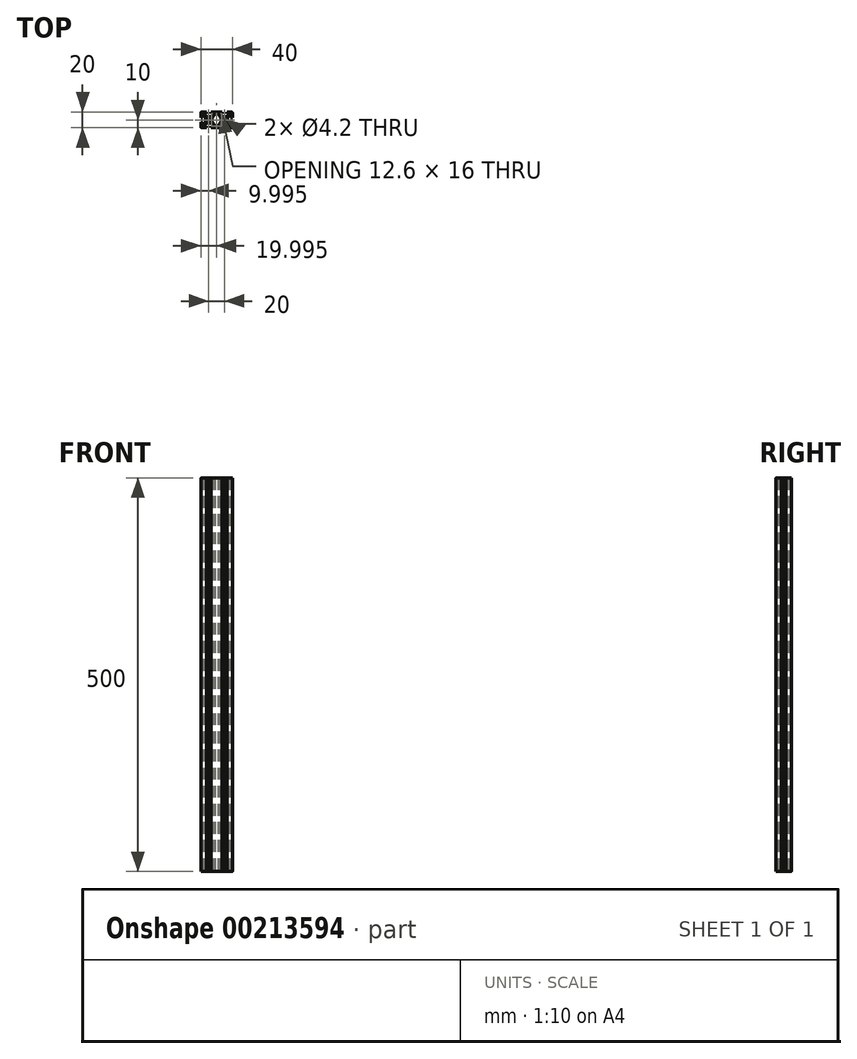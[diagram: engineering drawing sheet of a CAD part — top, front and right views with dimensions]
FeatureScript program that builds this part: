
annotation { "Feature Type Name" : "Feature", "Feature Type Description" : "" }
export const myFeature = defineFeature(function(context is Context, id is Id, definition is map)
    precondition{}
    {
        {
            var Q0;
            Q0=qCreatedBy(makeId("Top.planeOp"),FACE);
            var sketch = newSketch(context, id + "F0", { "sketchPlane" : qUnion([Q0])});
            skLineSegment(sketch, "E0.MirrorCS", {"start": v(6.14, -0.52) * mm, "end": v(6.44, 0) * mm});
            skLineSegment(sketch, "E1.MirrorCS", {"start": v(13.84, 0) * mm, "end": v(14.14, -0.52) * mm});
            skLineSegment(sketch, "E2.MirrorCS", {"start": v(10.65, -4) * mm, "end": v(10.14, -3.7) * mm});
            skLineSegment(sketch, "E3.MirrorCS", {"start": v(10.14, -3.7) * mm, "end": v(9.62, -4) * mm});
            skLineSegment(sketch, "E4.MirrorCS", {"start": v(4.14, -8) * mm, "end": v(7.14, -8) * mm});
            skLineSegment(sketch, "E5.MirrorCS", {"start": v(6.14, -2.94) * mm, "end": v(6.14, -0.52) * mm});
            skLineSegment(sketch, "E6.MirrorCS", {"start": v(16.14, -7.06) * mm, "end": v(13.07, -4) * mm});
            skLineSegment(sketch, "E7.MirrorCS", {"start": v(7.14, -8) * mm, "end": v(7.14, -10) * mm});
            skLineSegment(sketch, "E8.MirrorCS", {"start": v(20.14, -3) * mm, "end": v(20.14, -9) * mm});
            skLineSegment(sketch, "E9.MirrorCS", {"start": v(9.62, -4) * mm, "end": v(7.2, -4) * mm});
            skArc(sketch, "E10.MirrorCS", {"start": v(20.14, -9) * mm, "mid": v(19.84, -9.7) * mm, "end": v(19.14, -10) * mm});
            skLineSegment(sketch, "E11.MirrorCS", {"start": v(19.14, -10) * mm, "end": v(13.14, -10) * mm});
            skLineSegment(sketch, "E12.MirrorCS", {"start": v(13.07, -4) * mm, "end": v(10.65, -4) * mm});
            skLineSegment(sketch, "E13.MirrorCS", {"start": v(13.14, -10) * mm, "end": v(13.14, -8) * mm});
            skLineSegment(sketch, "E14.MirrorCS", {"start": v(14.14, -0.52) * mm, "end": v(14.14, -2.94) * mm});
            skLineSegment(sketch, "E15.MirrorCS", {"start": v(14.14, -2.94) * mm, "end": v(17.2, -6) * mm});
            skLineSegment(sketch, "E16.MirrorCS", {"start": v(17.2, -6) * mm, "end": v(18.14, -6) * mm});
            skLineSegment(sketch, "E17.MirrorCS", {"start": v(18.14, -6) * mm, "end": v(18.14, -3) * mm});
            skLineSegment(sketch, "E18.MirrorCS", {"start": v(18.14, -3) * mm, "end": v(20.14, -3) * mm});
            skLineSegment(sketch, "E19.MirrorCS", {"start": v(7.2, -4) * mm, "end": v(4.14, -7.06) * mm});
            skLineSegment(sketch, "E20.MirrorCS", {"start": v(13.14, -8) * mm, "end": v(16.14, -8) * mm});
            skLineSegment(sketch, "E21.MirrorCS", {"start": v(4.14, -7.06) * mm, "end": v(4.14, -8) * mm});
            skLineSegment(sketch, "E22.MirrorCS", {"start": v(16.14, -8) * mm, "end": v(16.14, -7.06) * mm});
            skLineSegment(sketch, "E23.MirrorCS", {"start": v(3.07, -6) * mm, "end": v(6.14, -2.94) * mm});
            skCircle(sketch, "E24", {"center": v(10.14, 0) * mm, "radius": 2.1 * mm});
            skLineSegment(sketch, "E25", {"start": v(3.07, -6) * mm, "end": v(2.01, -7.06) * mm});
            skLineSegment(sketch, "E26", {"start": v(2.01, -7.06) * mm, "end": v(2.01, -8) * mm});
            skLineSegment(sketch, "E27.MirrorCS", {"start": v(-10.38, -4) * mm, "end": v(-9.86, -3.7) * mm});
            skLineSegment(sketch, "E28.MirrorCS", {"start": v(-9.86, -3.7) * mm, "end": v(-9.35, -4) * mm});
            skLineSegment(sketch, "E29.MirrorCS", {"start": v(-13.56, 0) * mm, "end": v(-13.86, -0.52) * mm});
            skLineSegment(sketch, "E30.MirrorCS", {"start": v(-5.86, -0.52) * mm, "end": v(-6.16, 0) * mm});
            skLineSegment(sketch, "E31.MirrorCS", {"start": v(-12.86, -8) * mm, "end": v(-15.86, -8) * mm});
            skLineSegment(sketch, "E32.MirrorCS", {"start": v(-6.86, -8) * mm, "end": v(-6.86, -10) * mm});
            skLineSegment(sketch, "E33.MirrorCS", {"start": v(-19.86, -3) * mm, "end": v(-19.86, -9) * mm});
            skArc(sketch, "E34.MirrorCS", {"start": v(-19.86, -9) * mm, "mid": v(-19.57, -9.7) * mm, "end": v(-18.86, -10) * mm});
            skLineSegment(sketch, "E35.MirrorCS", {"start": v(-9.35, -4) * mm, "end": v(-6.93, -4) * mm});
            skLineSegment(sketch, "E36.MirrorCS", {"start": v(-18.86, -10) * mm, "end": v(-12.86, -10) * mm});
            skCircle(sketch, "E37.MirrorC", {"center": v(-9.86, 0) * mm, "radius": 2.1 * mm});
            skLineSegment(sketch, "E38.MirrorCS", {"start": v(-12.8, -4) * mm, "end": v(-10.38, -4) * mm});
            skLineSegment(sketch, "E39.MirrorCS", {"start": v(-17.86, -6) * mm, "end": v(-17.86, -3) * mm});
            skLineSegment(sketch, "E40.MirrorCS", {"start": v(-15.86, -8) * mm, "end": v(-15.86, -7.06) * mm});
            skLineSegment(sketch, "E41.MirrorCS", {"start": v(-13.86, -0.52) * mm, "end": v(-13.86, -2.94) * mm});
            skLineSegment(sketch, "E42.MirrorCS", {"start": v(-17.86, -3) * mm, "end": v(-19.86, -3) * mm});
            skLineSegment(sketch, "E43.MirrorCS", {"start": v(-13.86, -2.94) * mm, "end": v(-16.93, -6) * mm});
            skLineSegment(sketch, "E44.MirrorCS", {"start": v(-3.86, -8) * mm, "end": v(-6.86, -8) * mm});
            skLineSegment(sketch, "E45.MirrorCS", {"start": v(-15.86, -7.06) * mm, "end": v(-12.8, -4) * mm});
            skLineSegment(sketch, "E46.MirrorCS", {"start": v(-5.86, -2.94) * mm, "end": v(-5.86, -0.52) * mm});
            skLineSegment(sketch, "E47.MirrorCS", {"start": v(-6.93, -4) * mm, "end": v(-3.86, -7.06) * mm});
            skLineSegment(sketch, "E48.MirrorCS", {"start": v(-16.93, -6) * mm, "end": v(-17.86, -6) * mm});
            skLineSegment(sketch, "E49.MirrorCS", {"start": v(-1.74, -7.06) * mm, "end": v(-1.74, -8) * mm});
            skLineSegment(sketch, "E50.MirrorCS", {"start": v(-3.86, -7.06) * mm, "end": v(-3.86, -8) * mm});
            skLineSegment(sketch, "E51.MirrorCS", {"start": v(-2.8, -6) * mm, "end": v(-1.74, -7.06) * mm});
            skLineSegment(sketch, "E52.MirrorCS", {"start": v(-2.8, -6) * mm, "end": v(-5.86, -2.94) * mm});
            skLineSegment(sketch, "E53.MirrorCS", {"start": v(-12.86, -10) * mm, "end": v(-12.86, -8) * mm});
            skLineSegment(sketch, "E54.MirrorCS", {"start": v(10.14, 3.7) * mm, "end": v(9.62, 4) * mm});
            skLineSegment(sketch, "E55.MirrorCS", {"start": v(-10.38, 4) * mm, "end": v(-9.86, 3.7) * mm});
            skLineSegment(sketch, "E56.MirrorCS", {"start": v(10.65, 4) * mm, "end": v(10.14, 3.7) * mm});
            skLineSegment(sketch, "E57.MirrorCS", {"start": v(-9.86, 3.7) * mm, "end": v(-9.35, 4) * mm});
            skLineSegment(sketch, "E58.MirrorCS", {"start": v(13.84, 0) * mm, "end": v(14.14, 0.52) * mm});
            skLineSegment(sketch, "E59.MirrorCS", {"start": v(6.14, 0.52) * mm, "end": v(6.44, 0) * mm});
            skLineSegment(sketch, "E60.MirrorCS", {"start": v(-5.86, 0.52) * mm, "end": v(-6.16, 0) * mm});
            skLineSegment(sketch, "E61.MirrorCS", {"start": v(-13.56, 0) * mm, "end": v(-13.86, 0.52) * mm});
            skLineSegment(sketch, "E62.MirrorCS", {"start": v(-18.86, 10) * mm, "end": v(-12.86, 10) * mm});
            skLineSegment(sketch, "E63.MirrorCS", {"start": v(16.14, 7.06) * mm, "end": v(13.07, 4) * mm});
            skLineSegment(sketch, "E64.MirrorCS", {"start": v(6.14, 2.94) * mm, "end": v(6.14, 0.52) * mm});
            skLineSegment(sketch, "E65.MirrorCS", {"start": v(-3.86, 8) * mm, "end": v(-6.86, 8) * mm});
            skLineSegment(sketch, "E66.MirrorCS", {"start": v(4.14, 8) * mm, "end": v(7.14, 8) * mm});
            skLineSegment(sketch, "E67.MirrorCS", {"start": v(-15.86, 8) * mm, "end": v(-15.86, 7.06) * mm});
            skLineSegment(sketch, "E68.MirrorCS", {"start": v(-3.86, 7.06) * mm, "end": v(-3.86, 8) * mm});
            skArc(sketch, "E69.MirrorCS", {"start": v(20.14, 9) * mm, "mid": v(19.84, 9.7) * mm, "end": v(19.14, 10) * mm});
            skLineSegment(sketch, "E70.MirrorCS", {"start": v(14.14, 2.94) * mm, "end": v(17.2, 6) * mm});
            skLineSegment(sketch, "E71.MirrorCS", {"start": v(3.07, 6) * mm, "end": v(6.14, 2.94) * mm});
            skLineSegment(sketch, "E72.MirrorCS", {"start": v(-9.35, 4) * mm, "end": v(-6.93, 4) * mm});
            skLineSegment(sketch, "E73.MirrorCS", {"start": v(14.14, 0.52) * mm, "end": v(14.14, 2.94) * mm});
            skLineSegment(sketch, "E74.MirrorCS", {"start": v(-2.8, 6) * mm, "end": v(-5.86, 2.94) * mm});
            skLineSegment(sketch, "E75.MirrorCS", {"start": v(-17.86, 6) * mm, "end": v(-17.86, 3) * mm});
            skLineSegment(sketch, "E76.MirrorCS", {"start": v(16.14, 8) * mm, "end": v(16.14, 7.06) * mm});
            skLineSegment(sketch, "E77.MirrorCS", {"start": v(-15.86, 7.06) * mm, "end": v(-12.8, 4) * mm});
            skLineSegment(sketch, "E78.MirrorCS", {"start": v(18.14, 3) * mm, "end": v(20.14, 3) * mm});
            skLineSegment(sketch, "E79.MirrorCS", {"start": v(19.14, 10) * mm, "end": v(13.14, 10) * mm});
            skLineSegment(sketch, "E80.MirrorCS", {"start": v(4.14, 7.06) * mm, "end": v(4.14, 8) * mm});
            skLineSegment(sketch, "E81.MirrorCS", {"start": v(-12.86, 8) * mm, "end": v(-15.86, 8) * mm});
            skLineSegment(sketch, "E82.MirrorCS", {"start": v(-5.86, 2.94) * mm, "end": v(-5.86, 0.52) * mm});
            skLineSegment(sketch, "E83.MirrorCS", {"start": v(13.07, 4) * mm, "end": v(10.65, 4) * mm});
            skLineSegment(sketch, "E84.MirrorCS", {"start": v(-13.86, 2.94) * mm, "end": v(-16.93, 6) * mm});
            skLineSegment(sketch, "E85.MirrorCS", {"start": v(13.14, 8) * mm, "end": v(16.14, 8) * mm});
            skLineSegment(sketch, "E86.MirrorCS", {"start": v(-13.86, 0.52) * mm, "end": v(-13.86, 2.94) * mm});
            skLineSegment(sketch, "E87.MirrorCS", {"start": v(-6.86, 8) * mm, "end": v(-6.86, 10) * mm});
            skLineSegment(sketch, "E88.MirrorCS", {"start": v(20.14, 3) * mm, "end": v(20.14, 9) * mm});
            skLineSegment(sketch, "E89.MirrorCS", {"start": v(-12.8, 4) * mm, "end": v(-10.38, 4) * mm});
            skLineSegment(sketch, "E90.MirrorCS", {"start": v(-12.86, 10) * mm, "end": v(-12.86, 8) * mm});
            skLineSegment(sketch, "E91.MirrorCS", {"start": v(-6.93, 4) * mm, "end": v(-3.86, 7.06) * mm});
            skLineSegment(sketch, "E92.MirrorCS", {"start": v(9.62, 4) * mm, "end": v(7.2, 4) * mm});
            skLineSegment(sketch, "E93.MirrorCS", {"start": v(13.14, 10) * mm, "end": v(13.14, 8) * mm});
            skLineSegment(sketch, "E94.MirrorCS", {"start": v(-16.93, 6) * mm, "end": v(-17.86, 6) * mm});
            skLineSegment(sketch, "E95.MirrorCS", {"start": v(-19.86, 3) * mm, "end": v(-19.86, 9) * mm});
            skLineSegment(sketch, "E96.MirrorCS", {"start": v(3.07, 6) * mm, "end": v(2.01, 7.06) * mm});
            skLineSegment(sketch, "E97.MirrorCS", {"start": v(-17.86, 3) * mm, "end": v(-19.86, 3) * mm});
            skLineSegment(sketch, "E98.MirrorCS", {"start": v(-1.74, 7.06) * mm, "end": v(-1.74, 8) * mm});
            skLineSegment(sketch, "E99.MirrorCS", {"start": v(2.01, 7.06) * mm, "end": v(2.01, 8) * mm});
            skLineSegment(sketch, "E100.MirrorCS", {"start": v(18.14, 6) * mm, "end": v(18.14, 3) * mm});
            skArc(sketch, "E101.MirrorCS", {"start": v(-19.86, 9) * mm, "mid": v(-19.57, 9.7) * mm, "end": v(-18.86, 10) * mm});
            skLineSegment(sketch, "E102.MirrorCS", {"start": v(-2.8, 6) * mm, "end": v(-1.74, 7.06) * mm});
            skLineSegment(sketch, "E103.MirrorCS", {"start": v(7.14, 8) * mm, "end": v(7.14, 10) * mm});
            skLineSegment(sketch, "E104.MirrorCS", {"start": v(17.2, 6) * mm, "end": v(18.14, 6) * mm});
            skLineSegment(sketch, "E105.MirrorCS", {"start": v(7.2, 4) * mm, "end": v(4.14, 7.06) * mm});
            skLineSegment(sketch, "E106", {"start": v(7.14, -10) * mm, "end": v(-6.86, -10) * mm});
            skLineSegment(sketch, "E107", {"start": v(-1.74, -8) * mm, "end": v(2.01, -8) * mm});
            skLineSegment(sketch, "E108", {"start": v(-1.74, 8) * mm, "end": v(2.01, 8) * mm});
            skLineSegment(sketch, "E109", {"start": v(-6.86, 10) * mm, "end": v(7.14, 10) * mm});
            skLineSegment(sketch, "E110", {"start": v(-9.86, 0) * mm, "end": v(-19.86, 0) * mm, "construction": true});
            skSolve(sketch);
        }
        {
            var Q0;
            Q0=makeQuery(id+"F0.imprint","IMPRINT",FACE,{"disambiguationData":[TD([[makeQuery(id+"F0.imprint","IMPRINT",EDGE,{"derivedFrom":sQuery(id+"F0.wireOp",EDGE,"E0.MirrorCS")}),-1.0]])]});
            extrude(context, id + "F1", {"entities" : qUnion([Q0]), "depth" : 500 * mm});
        }
    });
